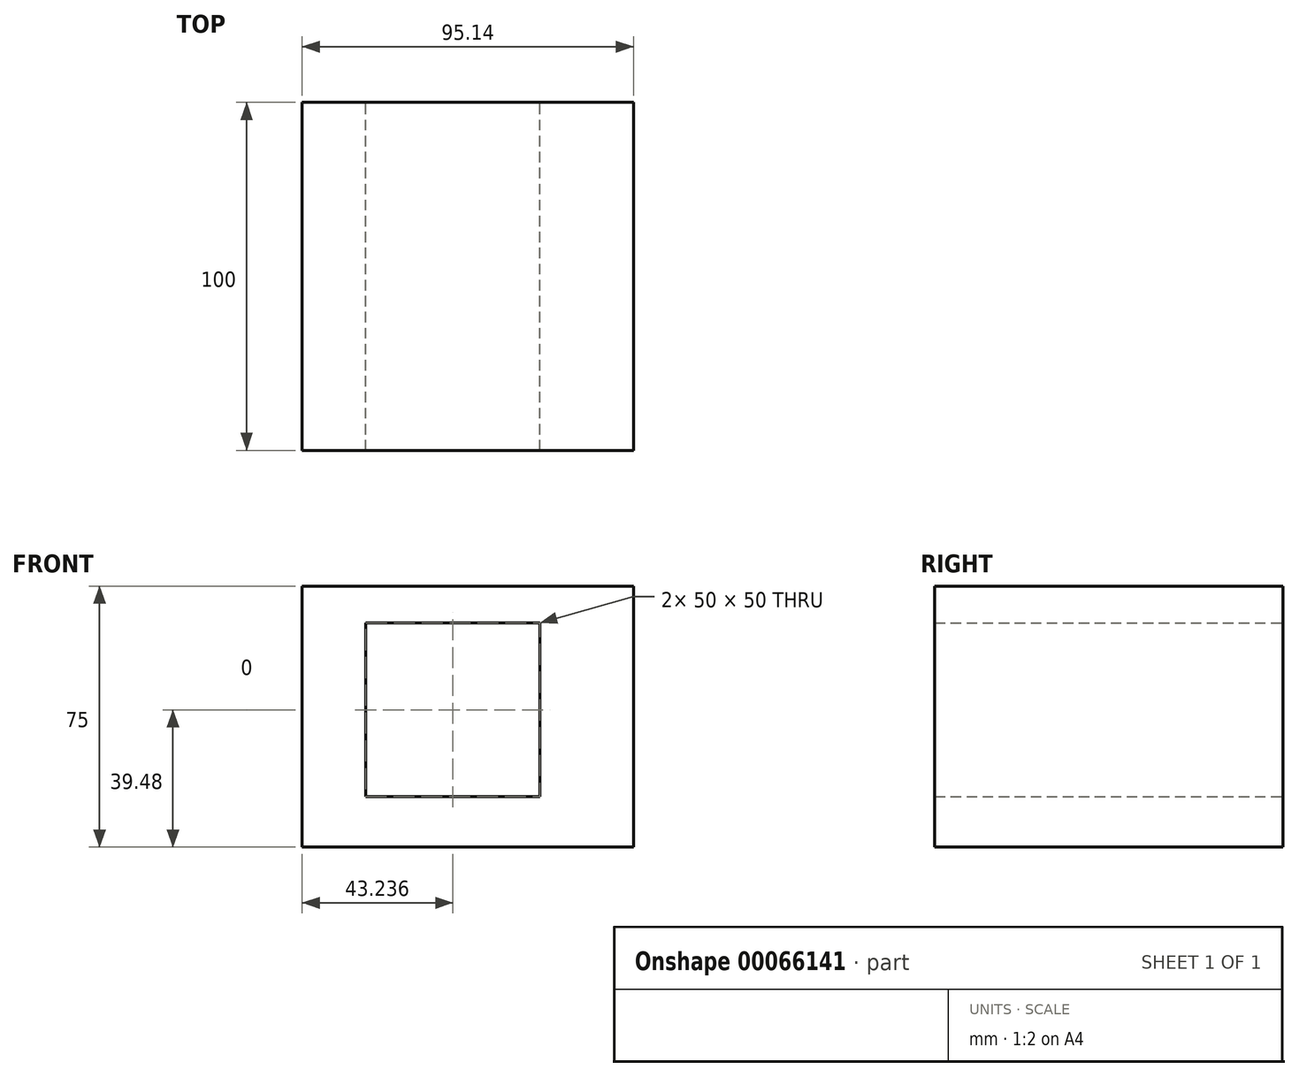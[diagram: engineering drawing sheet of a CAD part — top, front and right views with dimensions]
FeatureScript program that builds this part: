
annotation { "Feature Type Name" : "Feature", "Feature Type Description" : "" }
export const myFeature = defineFeature(function(context is Context, id is Id, definition is map)
    precondition{}
    {
        {
            var Q0;
            Q0=qCreatedBy(makeId("Front.planeOp"),FACE);
            var sketch = newSketch(context, id + "F0", { "sketchPlane" : qUnion([Q0])});
            skLineSegment(sketch, "E0.bottom", {"start": v(-45.21, 23.2) * mm, "end": v(4.79, 23.2) * mm});
            skLineSegment(sketch, "E0.top", {"start": v(-45.21, -26.8) * mm, "end": v(4.79, -26.8) * mm});
            skLineSegment(sketch, "E0.left", {"start": v(-45.21, 23.2) * mm, "end": v(-45.21, -26.8) * mm});
            skLineSegment(sketch, "E0.right", {"start": v(4.79, 23.2) * mm, "end": v(4.79, -26.8) * mm});
            skLineSegment(sketch, "E1.bottom", {"start": v(-63.45, 33.73) * mm, "end": v(31.69, 33.73) * mm});
            skLineSegment(sketch, "E1.top", {"start": v(-63.45, -41.27) * mm, "end": v(31.69, -41.27) * mm});
            skLineSegment(sketch, "E1.left", {"start": v(-63.45, 33.73) * mm, "end": v(-63.45, -41.27) * mm});
            skLineSegment(sketch, "E1.right", {"start": v(31.69, 33.73) * mm, "end": v(31.69, -41.27) * mm});
            skSolve(sketch);
        }
        {
            var Q0;
            Q0 = qSketchRegion(id + "F0", true);
            extrude(context, id + "F1", {"entities" : qUnion([Q0]), "depth" : 100 * mm});
        }
    });
